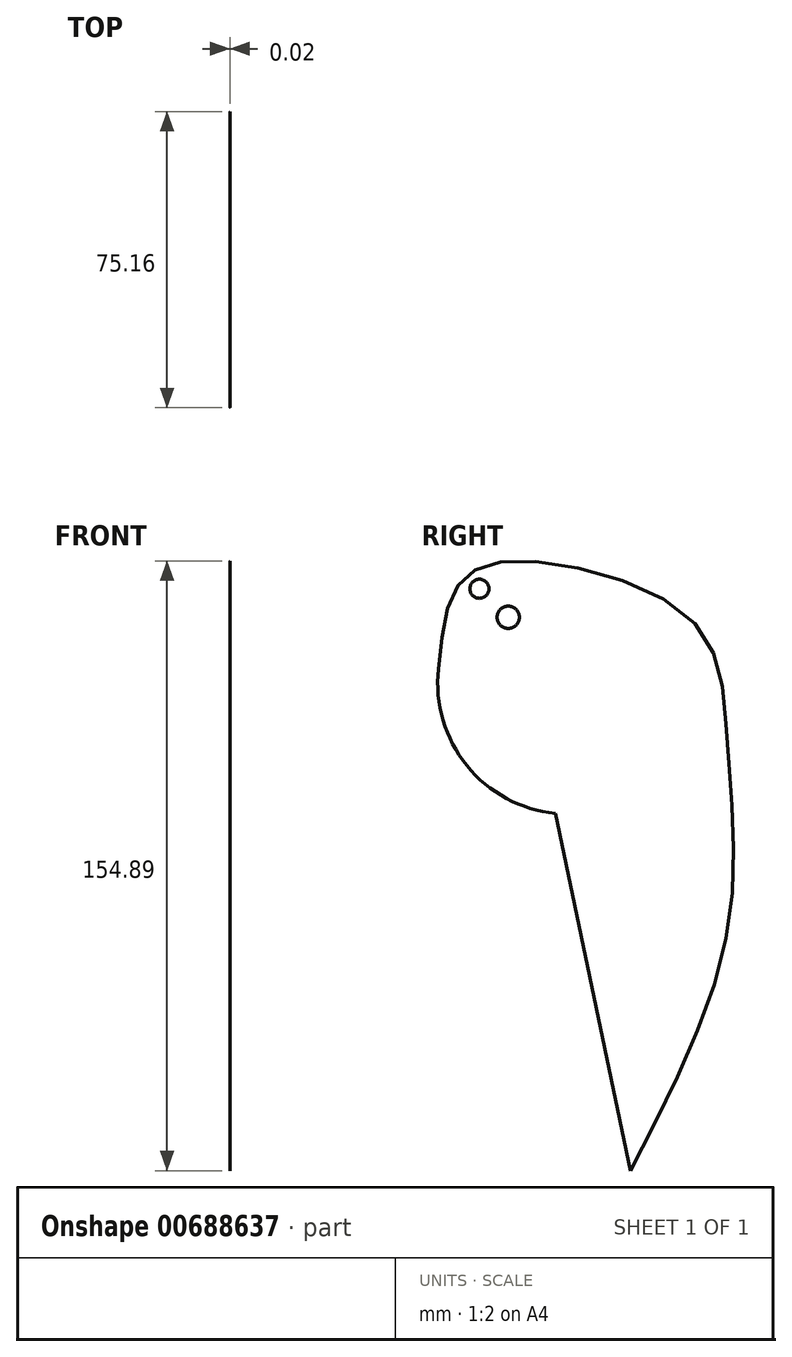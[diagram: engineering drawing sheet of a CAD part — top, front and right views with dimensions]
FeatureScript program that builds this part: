
annotation { "Feature Type Name" : "Feature", "Feature Type Description" : "" }
export const myFeature = defineFeature(function(context is Context, id is Id, definition is map)
    precondition{}
    {
        {
            var Q0;
            Q0=qCreatedBy(makeId("Right.planeOp"),FACE);
            var sketch = newSketch(context, id + "F0", { "sketchPlane" : qUnion([Q0])});
            skLineSegment(sketch, "E0", {"start": v(-43.67, 38.46) * mm, "end": v(-24.6, -52.29) * mm});
            skArc(sketch, "E1", {"start": v(-73.35, 75.12) * mm, "mid": v(-66.11, 50.63) * mm, "end": v(-43.67, 38.46) * mm});
            skFitSpline(sketch, "E2", {"points": [v(-73.35, 75.12) * mm, v(-68.64, 96.11) * mm, v(-53.19, 102.6) * mm, v(-9.11, 87.68) * mm, v(0, 56.57) * mm, v(0, 8.1) * mm, v(-24.6, -52.29) * mm], "startDerivative": vector(17.3, 187.95) * mm, "endDerivative": vector(-141.65, -273.92) * mm});
            skSolve(sketch);
        }
        {
            var Q0;
            Q0=makeQuery(id+"F0.imprint","IMPRINT",FACE,{"disambiguationData":[TD([[makeQuery(id+"F0.imprint","IMPRINT",EDGE,{"derivedFrom":sQuery(id+"F0.wireOp",EDGE,"E0")}),1.0]])]});
            extrude(context, id + "F1", {"entities" : qUnion([Q0]), "depth" : 1 / 50.8 * mm, "offsetDistance" : 25.4 * mm});
        }
        {
            var Q0;
            Q0=makeQuery(id+"F1.opExtrude","CAP_FACE",FACE,{"disambiguationData":[OSD([sQuery(id+"F0.wireOp",EDGE,"E0"),sQuery(id+"F0.wireOp",EDGE,"E1"),sQuery(id+"F0.wireOp",EDGE,"E2")])],"isStart":false});
            var sketch = newSketch(context, id + "F2", { "sketchPlane" : qUnion([Q0])});
            skCircle(sketch, "E3", {"center": v(-62.93, 95.56) * mm, "radius": 2.43 * mm});
            skSolve(sketch);
        }
        {
            var Q0;
            Q0 = qSketchRegion(id + "F2", true);
            extrude(context, id + "F3", {"entities" : qUnion([Q0]), "operationType" : NewBodyOperationType.REMOVE, "oppositeDirection" : true, "depth" : 25.4 * mm, "offsetDistance" : 25.4 * mm});
        }
        {
            var Q0;
            Q0=makeQuery(id+"F1.opExtrude","CAP_FACE",FACE,{"disambiguationData":[OSD([sQuery(id+"F0.wireOp",EDGE,"E0"),sQuery(id+"F0.wireOp",EDGE,"E1"),sQuery(id+"F0.wireOp",EDGE,"E2")])],"isStart":false});
            var sketch = newSketch(context, id + "F4", { "sketchPlane" : qUnion([Q0])});
            skCircle(sketch, "E4", {"center": v(-55.6, 88.3) * mm, "radius": 2.83 * mm});
            skSolve(sketch);
        }
        {
            var Q0;
            Q0 = qSketchRegion(id + "F4", true);
            extrude(context, id + "F5", {"entities" : qUnion([Q0]), "operationType" : NewBodyOperationType.REMOVE, "oppositeDirection" : true, "depth" : 25.4 * mm, "offsetDistance" : 25.4 * mm});
        }
    });
